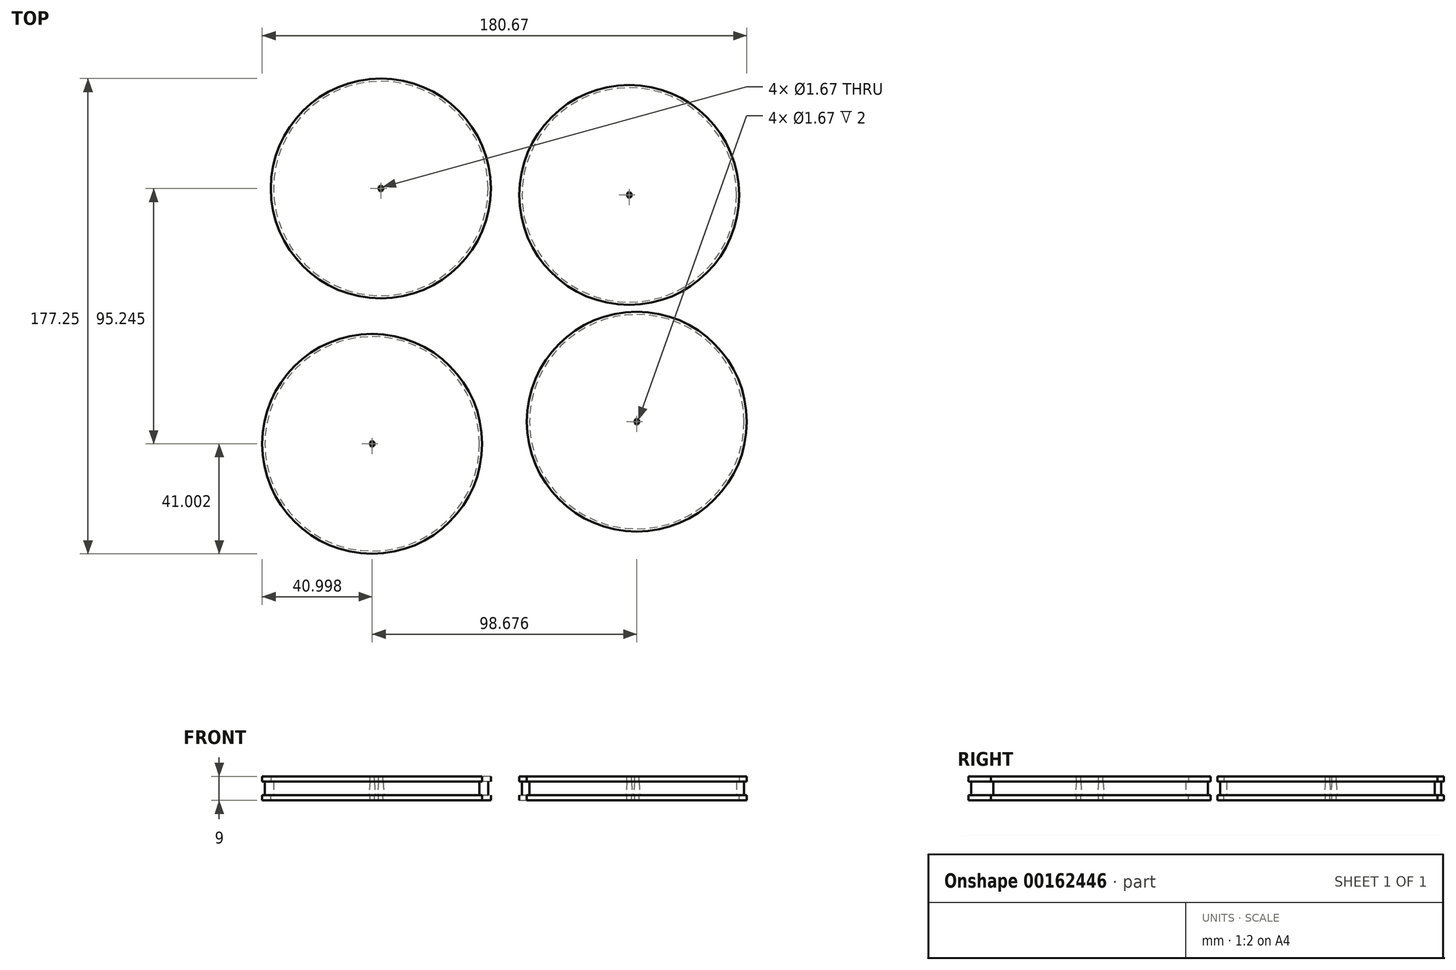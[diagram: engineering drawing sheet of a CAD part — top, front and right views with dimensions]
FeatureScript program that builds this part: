
annotation { "Feature Type Name" : "Feature", "Feature Type Description" : "" }
export const myFeature = defineFeature(function(context is Context, id is Id, definition is map)
    precondition{}
    {
        {
            var Q0;
            Q0=qCreatedBy(makeId("Top.planeOp"),FACE);
            var sketch = newSketch(context, id + "F0", { "sketchPlane" : qUnion([Q0])});
            skCircle(sketch, "E0", {"center": v(-43.18, 36.83) * mm, "radius": 40 * mm});
            skCircle(sketch, "E1", {"center": v(49.44, 34.4) * mm, "radius": 40 * mm});
            skCircle(sketch, "E2", {"center": v(-46.41, -58.42) * mm, "radius": 40 * mm});
            skCircle(sketch, "E3", {"center": v(52.26, -50.14) * mm, "radius": 40 * mm});
            skSolve(sketch);
        }
        {
            var Q0;
            Q0 = qSketchRegion(id + "F0", true);
            extrude(context, id + "F1", {"entities" : qUnion([Q0]), "depth" : 5 * mm});
        }
        {
            var Q0;
            Q0=makeQuery(id+"F1.opExtrude","CAP_FACE",FACE,{"disambiguationData":[OSD([sQuery(id+"F0.wireOp",EDGE,"E0")])],"isStart":false});
            var sketch = newSketch(context, id + "F2", { "sketchPlane" : qUnion([Q0])});
            skCircle(sketch, "E4", {"center": v(-43.18, 36.83) * mm, "radius": 0.83 * mm});
            skSolve(sketch);
        }
        {
            var Q0;
            Q0 = qSketchRegion(id + "F2", true);
            extrude(context, id + "F3", {"entities" : qUnion([Q0]), "operationType" : NewBodyOperationType.REMOVE, "endBound" : BoundingType.THROUGH_ALL, "oppositeDirection" : true, "depth" : 25 * mm, "hasDraft" : true, "draftAngle" : 4 * degree});
        }
        {
            var Q0;
            Q0=makeQuery(id+"F1.opExtrude","CAP_FACE",FACE,{"disambiguationData":[OSD([sQuery(id+"F0.wireOp",EDGE,"E1")])],"isStart":false});
            var sketch = newSketch(context, id + "F4", { "sketchPlane" : qUnion([Q0])});
            skCircle(sketch, "E5", {"center": v(49.44, 34.4) * mm, "radius": 0.83 * mm});
            skSolve(sketch);
        }
        {
            var Q0;
            Q0 = qSketchRegion(id + "F4", true);
            extrude(context, id + "F5", {"entities" : qUnion([Q0]), "operationType" : NewBodyOperationType.REMOVE, "endBound" : BoundingType.THROUGH_ALL, "oppositeDirection" : true, "depth" : 25 * mm, "hasDraft" : true, "draftAngle" : 4 * degree});
        }
        {
            var Q0;
            Q0=makeQuery(id+"F1.opExtrude","CAP_FACE",FACE,{"disambiguationData":[OSD([sQuery(id+"F0.wireOp",EDGE,"E2")])],"isStart":false});
            var sketch = newSketch(context, id + "F6", { "sketchPlane" : qUnion([Q0])});
            skCircle(sketch, "E6", {"center": v(-46.41, -58.42) * mm, "radius": 0.84 * mm});
            skSolve(sketch);
        }
        {
            var Q0;
            Q0 = qSketchRegion(id + "F6", true);
            extrude(context, id + "F7", {"entities" : qUnion([Q0]), "operationType" : NewBodyOperationType.REMOVE, "endBound" : BoundingType.THROUGH_ALL, "oppositeDirection" : true, "depth" : 25 * mm, "hasDraft" : true, "draftAngle" : 4 * degree});
        }
        {
            var Q0;
            Q0=makeQuery(id+"F1.opExtrude","CAP_FACE",FACE,{"disambiguationData":[OSD([sQuery(id+"F0.wireOp",EDGE,"E3")])],"isStart":false});
            var sketch = newSketch(context, id + "F8", { "sketchPlane" : qUnion([Q0])});
            skCircle(sketch, "E7", {"center": v(52.26, -50.14) * mm, "radius": 0.83 * mm});
            skSolve(sketch);
        }
        {
            var Q0;
            Q0 = qSketchRegion(id + "F8", true);
            extrude(context, id + "F9", {"entities" : qUnion([Q0]), "operationType" : NewBodyOperationType.REMOVE, "endBound" : BoundingType.THROUGH_ALL, "oppositeDirection" : true, "depth" : 25 * mm, "hasDraft" : true, "draftAngle" : 4 * degree});
        }
        {
            var Q0;
            Q0=makeQuery(id+"F1.opExtrude","CAP_FACE",FACE,{"disambiguationData":[OSD([sQuery(id+"F0.wireOp",EDGE,"E0")])],"isStart":false});
            var sketch = newSketch(context, id + "F10", { "sketchPlane" : qUnion([Q0])});
            skCircle(sketch, "E8", {"center": v(-43.18, 36.83) * mm, "radius": 41 * mm});
            skSolve(sketch);
        }
        {
            var Q0;
            Q0=makeQuery(id+"F1.opExtrude","CAP_FACE",FACE,{"disambiguationData":[OSD([sQuery(id+"F0.wireOp",EDGE,"E1")])],"isStart":false});
            var sketch = newSketch(context, id + "F11", { "sketchPlane" : qUnion([Q0])});
            skCircle(sketch, "E9", {"center": v(49.44, 34.4) * mm, "radius": 41 * mm});
            skSolve(sketch);
        }
        {
            var Q0;
            Q0=makeQuery(id+"F1.opExtrude","CAP_FACE",FACE,{"disambiguationData":[OSD([sQuery(id+"F0.wireOp",EDGE,"E2")])],"isStart":false});
            var sketch = newSketch(context, id + "F12", { "sketchPlane" : qUnion([Q0])});
            skCircle(sketch, "E10", {"center": v(-46.41, -58.42) * mm, "radius": 41 * mm});
            skSolve(sketch);
        }
        {
            var Q0;
            Q0=makeQuery(id+"F1.opExtrude","CAP_FACE",FACE,{"disambiguationData":[OSD([sQuery(id+"F0.wireOp",EDGE,"E3")])],"isStart":false});
            var sketch = newSketch(context, id + "F13", { "sketchPlane" : qUnion([Q0])});
            skCircle(sketch, "E11", {"center": v(52.26, -50.14) * mm, "radius": 41 * mm});
            skSolve(sketch);
        }
        {
            var Q0;
            Q0 = qSketchRegion(id + "F13", true);
            var Q1;
            Q1 = qSketchRegion(id + "F12", true);
            var Q2;
            Q2 = qSketchRegion(id + "F11", true);
            var Q3;
            Q3 = qSketchRegion(id + "F10", true);
            extrude(context, id + "F14", {"entities" : qUnion([Q0, Q1, Q2, Q3]), "operationType" : NewBodyOperationType.ADD, "depth" : 2 * mm});
        }
        {
            var Q0;
            Q0=makeQuery(id+"F1.opExtrude","CAP_FACE",FACE,{"disambiguationData":[OSD([sQuery(id+"F0.wireOp",EDGE,"E2")])],"isStart":true});
            var sketch = newSketch(context, id + "F15", { "sketchPlane" : qUnion([Q0])});
            skCircle(sketch, "E12", {"center": v(-46.41, 58.42) * mm, "radius": 41 * mm});
            skSolve(sketch);
        }
        {
            var Q0;
            Q0=makeQuery(id+"F1.opExtrude","CAP_FACE",FACE,{"disambiguationData":[OSD([sQuery(id+"F0.wireOp",EDGE,"E3")])],"isStart":true});
            var sketch = newSketch(context, id + "F16", { "sketchPlane" : qUnion([Q0])});
            skCircle(sketch, "E13", {"center": v(52.26, 50.14) * mm, "radius": 41 * mm});
            skSolve(sketch);
        }
        {
            var Q0;
            Q0=makeQuery(id+"F1.opExtrude","CAP_FACE",FACE,{"disambiguationData":[OSD([sQuery(id+"F0.wireOp",EDGE,"E0")])],"isStart":true});
            var sketch = newSketch(context, id + "F17", { "sketchPlane" : qUnion([Q0])});
            skCircle(sketch, "E14", {"center": v(-43.18, -36.83) * mm, "radius": 41 * mm});
            skSolve(sketch);
        }
        {
            var Q0;
            Q0=makeQuery(id+"F1.opExtrude","CAP_FACE",FACE,{"disambiguationData":[OSD([sQuery(id+"F0.wireOp",EDGE,"E1")])],"isStart":true});
            var sketch = newSketch(context, id + "F18", { "sketchPlane" : qUnion([Q0])});
            skCircle(sketch, "E15", {"center": v(49.44, -34.4) * mm, "radius": 41 * mm});
            skSolve(sketch);
        }
        {
            var Q0;
            Q0 = qSketchRegion(id + "F15", true);
            var Q1;
            Q1 = qSketchRegion(id + "F16", true);
            var Q2;
            Q2 = qSketchRegion(id + "F17", true);
            var Q3;
            Q3 = qSketchRegion(id + "F18", true);
            extrude(context, id + "F19", {"entities" : qUnion([Q0, Q1, Q2, Q3]), "operationType" : NewBodyOperationType.ADD, "depth" : 2 * mm});
        }
        {
            var Q0;
            Q0=makeQuery(id+"F14.opExtrude","CAP_FACE",FACE,{"disambiguationData":[OSD([sQuery(id+"F10.wireOp",EDGE,"E8")])],"isStart":false});
            var sketch = newSketch(context, id + "F20", { "sketchPlane" : qUnion([Q0])});
            skCircle(sketch, "E16", {"center": v(-43.18, 36.83) * mm, "radius": 0.84 * mm});
            skSolve(sketch);
        }
        {
            var Q0;
            Q0=makeQuery(id+"F14.opExtrude","CAP_FACE",FACE,{"disambiguationData":[OSD([sQuery(id+"F12.wireOp",EDGE,"E10")])],"isStart":false});
            var sketch = newSketch(context, id + "F21", { "sketchPlane" : qUnion([Q0])});
            skCircle(sketch, "E17", {"center": v(-46.41, -58.42) * mm, "radius": 0.84 * mm});
            skSolve(sketch);
        }
        {
            var Q0;
            Q0=makeQuery(id+"F14.opExtrude","CAP_FACE",FACE,{"disambiguationData":[OSD([sQuery(id+"F13.wireOp",EDGE,"E11")])],"isStart":false});
            var sketch = newSketch(context, id + "F22", { "sketchPlane" : qUnion([Q0])});
            skCircle(sketch, "E18", {"center": v(52.26, -50.14) * mm, "radius": 0.84 * mm});
            skSolve(sketch);
        }
        {
            var Q0;
            Q0=makeQuery(id+"F14.opExtrude","CAP_FACE",FACE,{"disambiguationData":[OSD([sQuery(id+"F11.wireOp",EDGE,"E9")])],"isStart":false});
            var sketch = newSketch(context, id + "F23", { "sketchPlane" : qUnion([Q0])});
            skCircle(sketch, "E19", {"center": v(49.44, 34.4) * mm, "radius": 0.84 * mm});
            skSolve(sketch);
        }
        {
            var Q0;
            Q0 = qSketchRegion(id + "F20", true);
            var Q1;
            Q1 = qSketchRegion(id + "F21", true);
            var Q2;
            Q2 = qSketchRegion(id + "F22", true);
            var Q3;
            Q3 = qSketchRegion(id + "F23", true);
            extrude(context, id + "F24", {"entities" : qUnion([Q0, Q1, Q2, Q3]), "operationType" : NewBodyOperationType.REMOVE, "endBound" : BoundingType.THROUGH_ALL, "oppositeDirection" : true, "depth" : 25 * mm});
        }
    });
